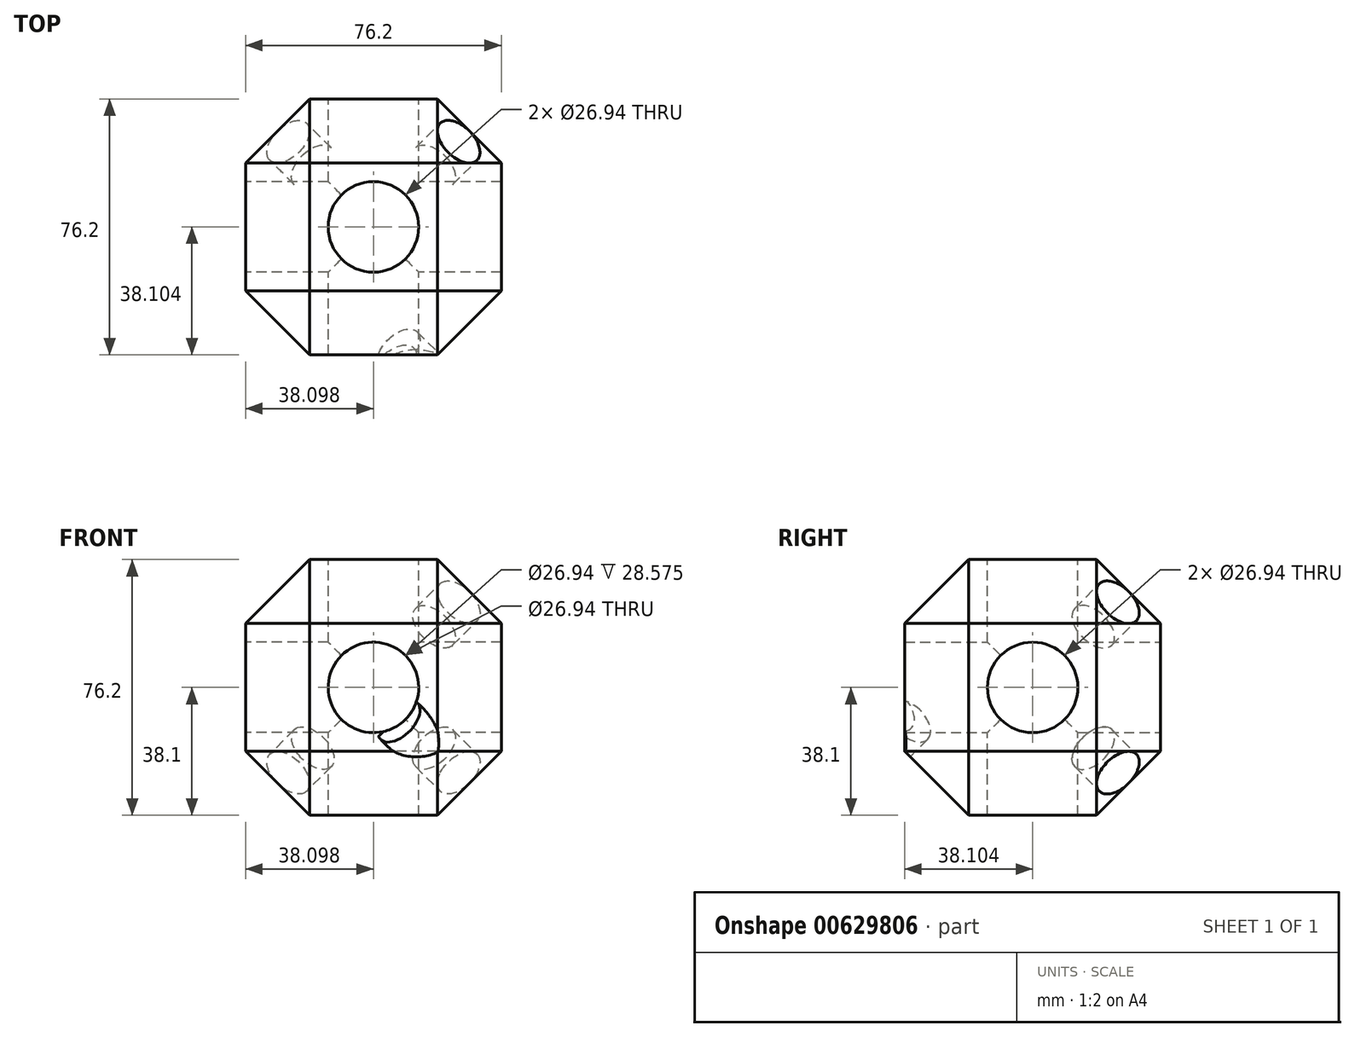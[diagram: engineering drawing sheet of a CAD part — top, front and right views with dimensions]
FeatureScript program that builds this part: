
annotation { "Feature Type Name" : "Feature", "Feature Type Description" : "" }
export const myFeature = defineFeature(function(context is Context, id is Id, definition is map)
    precondition{}
    {
        {
            var Q0;
            Q0=qCreatedBy(makeId("Top.planeOp"),FACE);
            var sketch = newSketch(context, id + "F0", { "sketchPlane" : qUnion([Q0])});
            skLineSegment(sketch, "E0.rect.bottom", {"start": v(29.23, 73.8) * mm, "end": v(-46.97, 73.8) * mm});
            skLineSegment(sketch, "E0.rect.top", {"start": v(29.23, -2.4) * mm, "end": v(-46.97, -2.4) * mm});
            skLineSegment(sketch, "E0.rect.left", {"start": v(29.23, 73.8) * mm, "end": v(29.23, -2.4) * mm});
            skLineSegment(sketch, "E0.rect.right", {"start": v(-46.97, 73.8) * mm, "end": v(-46.97, -2.4) * mm});
            skPoint(sketch, "E0.rect.middle", {"position": v(-8.87, 35.7) * mm});
            skSolve(sketch);
        }
        {
            var Q0;
            Q0=qSketchRegion(id+"F0",true);
            extrude(context, id + "F1", {"entities" : qUnion([Q0]), "depth" : 76.2 * mm});
        }
        {
            var Q0;
            Q0=makeQuery(id+"F1.opExtrude","SWEPT_FACE",FACE,{"disambiguationData":[OSD([sQuery(id+"F0.wireOp",EDGE,"E0.rect.right")])]});
            var Q1;
            Q1=makeQuery(id+"F1.opExtrude","SWEPT_FACE",FACE,{"disambiguationData":[OSD([sQuery(id+"F0.wireOp",EDGE,"E0.rect.bottom")])]});
            var Q2;
            Q2=makeQuery(id+"F1.opExtrude","SWEPT_FACE",FACE,{"disambiguationData":[OSD([sQuery(id+"F0.wireOp",EDGE,"E0.rect.top")])]});
            var Q3;
            Q3=makeQuery(id+"F1.opExtrude","CAP_FACE",FACE,{"disambiguationData":[OSD([sQuery(id+"F0.wireOp",EDGE,"E0.rect.bottom"),sQuery(id+"F0.wireOp",EDGE,"E0.rect.top"),sQuery(id+"F0.wireOp",EDGE,"E0.rect.left"),sQuery(id+"F0.wireOp",EDGE,"E0.rect.right")])],"isStart":true});
            var Q4;
            Q4=makeQuery(id+"F1.opExtrude","SWEPT_FACE",FACE,{"disambiguationData":[OSD([sQuery(id+"F0.wireOp",EDGE,"E0.rect.left")])]});
            chamfer(context, id + "F2", {"entities" : qUnion([Q0, Q1, Q2, Q3, Q4]), "width" : 19.05 * mm, "tangentPropagation" : true});
        }
        {
            var Q0;
            Q0=makeQuery(id+"F1.opExtrude","CAP_FACE",FACE,{"disambiguationData":[OSD([sQuery(id+"F0.wireOp",EDGE,"E0.rect.bottom"),sQuery(id+"F0.wireOp",EDGE,"E0.rect.top"),sQuery(id+"F0.wireOp",EDGE,"E0.rect.left"),sQuery(id+"F0.wireOp",EDGE,"E0.rect.right")])],"isStart":false});
            var sketch = newSketch(context, id + "F3", { "sketchPlane" : qUnion([Q0])});
            skCircle(sketch, "E1", {"center": v(-8.87, 35.7) * mm, "radius": 13.47 * mm});
            skPoint(sketch, "E1.first.point", {"position": v(-18.4, 45.22) * mm});
            skPoint(sketch, "E1.second.point", {"position": v(0.65, 45.22) * mm});
            skPoint(sketch, "E1.third.point", {"position": v(0.65, 26.17) * mm});
            skSolve(sketch);
        }
        {
            var Q0;
            Q0=qSketchRegion(id+"F3",true);
            extrude(context, id + "F4", {"entities" : qUnion([Q0]), "operationType" : NewBodyOperationType.REMOVE, "oppositeDirection" : true, "depth" : 127 * mm});
        }
        {
            var Q0;
            Q0=makeQuery(id+"F1.opExtrude","SWEPT_FACE",FACE,{"disambiguationData":[OSD([sQuery(id+"F0.wireOp",EDGE,"E0.rect.right")])]});
            var sketch = newSketch(context, id + "F5", { "sketchPlane" : qUnion([Q0])});
            skCircle(sketch, "E2", {"center": v(-35.7, 38.1) * mm, "radius": 13.47 * mm});
            skSolve(sketch);
        }
        {
            var Q0;
            Q0=qSketchRegion(id+"F5",true);
            var Q1;
            Q1=makeQuery(id+"F5.imprint","IMPRINT",FACE,{"disambiguationData":[TD([[makeQuery(id+"F5.imprint","IMPRINT",EDGE,{"derivedFrom":sQuery(id+"F5.wireOp",EDGE,"E2")}),1.0]])]});
            extrude(context, id + "F6", {"entities" : qUnion([Q0, Q1]), "operationType" : NewBodyOperationType.REMOVE, "oppositeDirection" : true, "depth" : 127 * mm});
        }
        {
            var Q0;
            Q0=makeQuery(id+"F1.opExtrude","SWEPT_FACE",FACE,{"disambiguationData":[OSD([sQuery(id+"F0.wireOp",EDGE,"E0.rect.bottom")])]});
            var sketch = newSketch(context, id + "F7", { "sketchPlane" : qUnion([Q0])});
            skCircle(sketch, "E3", {"center": v(8.87, 38.1) * mm, "radius": 13.47 * mm});
            skSolve(sketch);
        }
        {
            var Q0;
            Q0=qSketchRegion(id+"F7",true);
            extrude(context, id + "F8", {"entities" : qUnion([Q0]), "operationType" : NewBodyOperationType.REMOVE, "oppositeDirection" : true, "depth" : 127 * mm});
        }
        {
            var Q0;
            {var subQ0=sQuery(id+"F0.wireOp",EDGE,"E0.rect.bottom");var subQ1=sQuery(id+"F0.wireOp",EDGE,"E0.rect.left");Q0=makeQuery(id+"F2.opChamfer","BLEND_FACE",FACE,{"disambiguationData":[OSD([subQ0,subQ1]),TDD([makeQuery(id+"F1.opExtrude","CAP_VERTEX",VERTEX,{"disambiguationData":[OSD([subQ0,subQ1])],"isStart":true})])]});}
            var sketch = newSketch(context, id + "F9", { "sketchPlane" : qUnion([Q0])});
            skCircle(sketch, "E4", {"center": v(6.26, 52.18) * mm, "radius": 7.78 * mm});
            skPoint(sketch, "E4.first.point", {"position": v(2.37, 58.92) * mm});
            skPoint(sketch, "E4.second.point", {"position": v(14.04, 52.18) * mm});
            skPoint(sketch, "E4.third.point", {"position": v(2.37, 45.44) * mm});
            skSolve(sketch);
        }
        {
            var Q0;
            Q0=qSketchRegion(id+"F9",true);
            extrude(context, id + "F10", {"entities" : qUnion([Q0]), "operationType" : NewBodyOperationType.REMOVE, "oppositeDirection" : true, "depth" : 12.7 * mm});
        }
        {
            var Q0;
            {var subQ0=sQuery(id+"F0.wireOp",EDGE,"E0.rect.bottom");var subQ1=sQuery(id+"F0.wireOp",EDGE,"E0.rect.left");Q0=makeQuery(id+"F2.opChamfer","BLEND_FACE",FACE,{"disambiguationData":[OSD([subQ0,subQ1]),TDD([makeQuery(id+"F1.opExtrude","CAP_VERTEX",VERTEX,{"disambiguationData":[OSD([subQ0,subQ1])],"isStart":false})])]});}
            var sketch = newSketch(context, id + "F11", { "sketchPlane" : qUnion([Q0])});
            skCircle(sketch, "E5", {"center": v(37.37, 1.7) * mm, "radius": 7.78 * mm});
            skPoint(sketch, "E5.first.point", {"position": v(45.15, 1.7) * mm});
            skPoint(sketch, "E5.second.point", {"position": v(33.48, 8.44) * mm});
            skPoint(sketch, "E5.third.point", {"position": v(33.48, -5.03) * mm});
            skSolve(sketch);
        }
        {
            var Q0;
            {var subQ0=sQuery(id+"F11.wireOp",EDGE,"E5");var subQ1=sQuery(id+"F0.wireOp",EDGE,"E0.rect.bottom");var subQ2=sQuery(id+"F0.wireOp",EDGE,"E0.rect.left");var subQ3=makeQuery(id+"F1.opExtrude","CAP_VERTEX",VERTEX,{"disambiguationData":[OSD([subQ1,subQ2])],"isStart":false});var subQ6=makeQuery(id+"F11.imprint","INTERSECT",VERTEX,{"derivedFrom":[makeQuery(id+"F2.opChamfer","BLEND_EDGE",EDGE,{"blendedFrom":[subQ3,makeQuery(id+"F1.opExtrude","CAP_EDGE",EDGE,{"disambiguationData":[OSD([subQ2])],"isStart":false})],"blendedInto":[]}),subQ0]});Q0=makeQuery(id+"F11.imprint","IMPRINT",FACE,{"disambiguationData":[TD([[makeQuery(id+"F11.imprint","IMPRINT",EDGE,{"disambiguationData":[TD([[subQ6,1.0]])],"derivedFrom":subQ0}),1.0]])]});}
            extrude(context, id + "F12", {"entities" : qUnion([Q0]), "operationType" : NewBodyOperationType.REMOVE, "oppositeDirection" : true, "depth" : 12.7 * mm});
        }
        {
            var Q0;
            {var subQ0=sQuery(id+"F0.wireOp",EDGE,"E0.rect.bottom");var subQ1=sQuery(id+"F0.wireOp",EDGE,"E0.rect.right");Q0=makeQuery(id+"F2.opChamfer","BLEND_FACE",FACE,{"disambiguationData":[OSD([subQ0,subQ1]),TDD([makeQuery(id+"F1.opExtrude","CAP_VERTEX",VERTEX,{"disambiguationData":[OSD([subQ0,subQ1])],"isStart":false})])]});}
            var sketch = newSketch(context, id + "F13", { "sketchPlane" : qUnion([Q0])});
            skCircle(sketch, "E6", {"center": v(22.88, -1.7) * mm, "radius": 7.78 * mm});
            skPoint(sketch, "E6.first.point", {"position": v(19, -8.44) * mm});
            skPoint(sketch, "E6.second.point", {"position": v(19, 5.03) * mm});
            skPoint(sketch, "E6.third.point", {"position": v(30.66, -1.7) * mm});
            skSolve(sketch);
        }
        {
            var Q0;
            Q0=qSketchRegion(id+"F13",true);
            extrude(context, id + "F14", {"entities" : qUnion([Q0]), "operationType" : NewBodyOperationType.REMOVE, "oppositeDirection" : true, "depth" : 12.7 * mm});
        }
        {
            var Q0;
            {var subQ0=sQuery(id+"F0.wireOp",EDGE,"E0.rect.top");var subQ1=sQuery(id+"F0.wireOp",EDGE,"E0.rect.left");Q0=makeQuery(id+"F2.opChamfer","BLEND_FACE",FACE,{"disambiguationData":[OSD([subQ0,subQ1]),TDD([makeQuery(id+"F1.opExtrude","CAP_VERTEX",VERTEX,{"disambiguationData":[OSD([subQ0,subQ1])],"isStart":false})])]});}
            var sketch = newSketch(context, id + "F15", { "sketchPlane" : qUnion([Q0])});
            skCircle(sketch, "E7", {"center": v(41.08, 33.21) * mm, "radius": 7.78 * mm});
            skPoint(sketch, "E7.first.point", {"position": v(37.19, 39.95) * mm});
            skPoint(sketch, "E7.second.point", {"position": v(48.85, 33.21) * mm});
            skPoint(sketch, "E7.third.point", {"position": v(37.19, 26.48) * mm});
            skSolve(sketch);
        }
        {
            var Q0;
            {var subQ0=sQuery(id+"F15.wireOp",EDGE,"E7");var subQ1=sQuery(id+"F0.wireOp",EDGE,"E0.rect.top");var subQ2=sQuery(id+"F0.wireOp",EDGE,"E0.rect.left");var subQ3=makeQuery(id+"F1.opExtrude","CAP_VERTEX",VERTEX,{"disambiguationData":[OSD([subQ1,subQ2])],"isStart":false});var subQ6=makeQuery(id+"F15.imprint","INTERSECT",VERTEX,{"derivedFrom":[makeQuery(id+"F2.opChamfer","BLEND_EDGE",EDGE,{"blendedFrom":[subQ3,makeQuery(id+"F1.opExtrude","CAP_EDGE",EDGE,{"disambiguationData":[OSD([subQ1])],"isStart":false})],"blendedInto":[]}),subQ0]});Q0=makeQuery(id+"F15.imprint","IMPRINT",FACE,{"disambiguationData":[TD([[makeQuery(id+"F15.imprint","IMPRINT",EDGE,{"disambiguationData":[TD([[subQ6,1.0]])],"derivedFrom":subQ0}),1.0]])]});}
            extrude(context, id + "F16", {"entities" : qUnion([Q0]), "operationType" : NewBodyOperationType.REMOVE, "oppositeDirection" : true, "depth" : 12.7 * mm});
        }
        {
            var Q0;
            {var subQ0=sQuery(id+"F0.wireOp",EDGE,"E0.rect.top");var subQ1=sQuery(id+"F0.wireOp",EDGE,"E0.rect.left");Q0=makeQuery(id+"F2.opChamfer","BLEND_FACE",FACE,{"disambiguationData":[OSD([subQ0,subQ1]),TDD([makeQuery(id+"F1.opExtrude","CAP_VERTEX",VERTEX,{"disambiguationData":[OSD([subQ0,subQ1])],"isStart":true})])]});}
            var sketch = newSketch(context, id + "F17", { "sketchPlane" : qUnion([Q0])});
            skCircle(sketch, "E8", {"center": v(9.97, 20.67) * mm, "radius": 7.78 * mm});
            skPoint(sketch, "E8.first.point", {"position": v(17.74, 20.67) * mm});
            skPoint(sketch, "E8.second.point", {"position": v(6.08, 13.93) * mm});
            skPoint(sketch, "E8.third.point", {"position": v(6.08, 27.4) * mm});
            skSolve(sketch);
        }
        {
            var Q0;
            {var subQ0=sQuery(id+"F17.wireOp",EDGE,"E8");var subQ1=sQuery(id+"F0.wireOp",EDGE,"E0.rect.top");var subQ2=sQuery(id+"F0.wireOp",EDGE,"E0.rect.left");var subQ3=makeQuery(id+"F1.opExtrude","CAP_VERTEX",VERTEX,{"disambiguationData":[OSD([subQ1,subQ2])],"isStart":true});var subQ5=makeQuery(id+"F17.imprint","INTERSECT",VERTEX,{"derivedFrom":[makeQuery(id+"F2.opChamfer","BLEND_EDGE",EDGE,{"blendedFrom":[subQ3,makeQuery(id+"F1.opExtrude","CAP_EDGE",EDGE,{"disambiguationData":[OSD([subQ2])],"isStart":true})],"blendedInto":[]}),subQ0]});Q0=makeQuery(id+"F17.imprint","IMPRINT",FACE,{"disambiguationData":[TD([[makeQuery(id+"F17.imprint","IMPRINT",EDGE,{"disambiguationData":[TD([[subQ5,1.0]])],"derivedFrom":subQ0}),1.0]])]});}
            extrude(context, id + "F18", {"entities" : qUnion([Q0]), "operationType" : NewBodyOperationType.REMOVE, "oppositeDirection" : true, "depth" : 12.7 * mm});
        }
        {
            var Q0;
            {var subQ0=sQuery(id+"F0.wireOp",EDGE,"E0.rect.top");var subQ1=sQuery(id+"F0.wireOp",EDGE,"E0.rect.right");Q0=makeQuery(id+"F2.opChamfer","BLEND_FACE",FACE,{"disambiguationData":[OSD([subQ0,subQ1]),TDD([makeQuery(id+"F1.opExtrude","CAP_VERTEX",VERTEX,{"disambiguationData":[OSD([subQ0,subQ1])],"isStart":true})])]});}
            var sketch = newSketch(context, id + "F19", { "sketchPlane" : qUnion([Q0])});
            skCircle(sketch, "E9", {"center": v(-17.21, 33.21) * mm, "radius": 7.78 * mm});
            skPoint(sketch, "E9.first.point", {"position": v(-13.32, 26.48) * mm});
            skPoint(sketch, "E9.second.point", {"position": v(-24.99, 33.21) * mm});
            skPoint(sketch, "E9.third.point", {"position": v(-13.32, 39.95) * mm});
            skSolve(sketch);
        }
        {
            var Q0;
            {var subQ0=sQuery(id+"F19.wireOp",EDGE,"E9");var subQ1=sQuery(id+"F0.wireOp",EDGE,"E0.rect.top");var subQ2=sQuery(id+"F0.wireOp",EDGE,"E0.rect.right");var subQ3=makeQuery(id+"F1.opExtrude","CAP_VERTEX",VERTEX,{"disambiguationData":[OSD([subQ1,subQ2])],"isStart":true});var subQ6=makeQuery(id+"F19.imprint","INTERSECT",VERTEX,{"derivedFrom":[makeQuery(id+"F2.opChamfer","BLEND_EDGE",EDGE,{"blendedFrom":[subQ3,makeQuery(id+"F1.opExtrude","CAP_EDGE",EDGE,{"disambiguationData":[OSD([subQ2])],"isStart":true})],"blendedInto":[]}),subQ0]});Q0=makeQuery(id+"F19.imprint","IMPRINT",FACE,{"disambiguationData":[TD([[makeQuery(id+"F19.imprint","IMPRINT",EDGE,{"disambiguationData":[TD([[subQ6,-1.0]])],"derivedFrom":subQ0}),1.0]])]});}
            extrude(context, id + "F20", {"entities" : qUnion([Q0]), "operationType" : NewBodyOperationType.REMOVE, "oppositeDirection" : true, "depth" : 12.7 * mm});
        }
        {
            var Q0;
            {var subQ0=sQuery(id+"F0.wireOp",EDGE,"E0.rect.top");var subQ1=sQuery(id+"F0.wireOp",EDGE,"E0.rect.right");Q0=makeQuery(id+"F2.opChamfer","BLEND_FACE",FACE,{"disambiguationData":[OSD([subQ0,subQ1]),TDD([makeQuery(id+"F1.opExtrude","CAP_VERTEX",VERTEX,{"disambiguationData":[OSD([subQ0,subQ1])],"isStart":false})])]});}
            var sketch = newSketch(context, id + "F21", { "sketchPlane" : qUnion([Q0])});
            skCircle(sketch, "E10", {"center": v(-48.32, 20.67) * mm, "radius": 7.78 * mm});
            skPoint(sketch, "E10.first.point", {"position": v(-44.43, 13.93) * mm});
            skPoint(sketch, "E10.second.point", {"position": v(-44.43, 27.4) * mm});
            skPoint(sketch, "E10.third.point", {"position": v(-56.1, 20.67) * mm});
            skSolve(sketch);
        }
        {
            var Q0;
            {var subQ0=sQuery(id+"F21.wireOp",EDGE,"E10");var subQ1=sQuery(id+"F0.wireOp",EDGE,"E0.rect.top");var subQ2=sQuery(id+"F0.wireOp",EDGE,"E0.rect.right");var subQ3=makeQuery(id+"F1.opExtrude","CAP_VERTEX",VERTEX,{"disambiguationData":[OSD([subQ1,subQ2])],"isStart":false});var subQ6=makeQuery(id+"F21.imprint","INTERSECT",VERTEX,{"derivedFrom":[makeQuery(id+"F2.opChamfer","BLEND_EDGE",EDGE,{"blendedFrom":[subQ3,makeQuery(id+"F1.opExtrude","CAP_EDGE",EDGE,{"disambiguationData":[OSD([subQ2])],"isStart":false})],"blendedInto":[]}),subQ0]});Q0=makeQuery(id+"F21.imprint","IMPRINT",FACE,{"disambiguationData":[TD([[makeQuery(id+"F21.imprint","IMPRINT",EDGE,{"disambiguationData":[TD([[subQ6,1.0]])],"derivedFrom":subQ0}),1.0]])]});}
            extrude(context, id + "F22", {"entities" : qUnion([Q0]), "operationType" : NewBodyOperationType.REMOVE, "oppositeDirection" : true, "depth" : 12.7 * mm});
        }
        {
            var Q0;
            {var subQ0=sQuery(id+"F0.wireOp",EDGE,"E0.rect.bottom");var subQ1=sQuery(id+"F0.wireOp",EDGE,"E0.rect.right");Q0=makeQuery(id+"F2.opChamfer","BLEND_FACE",FACE,{"disambiguationData":[OSD([subQ0,subQ1]),TDD([makeQuery(id+"F1.opExtrude","CAP_VERTEX",VERTEX,{"disambiguationData":[OSD([subQ0,subQ1])],"isStart":true})])]});}
            var sketch = newSketch(context, id + "F23", { "sketchPlane" : qUnion([Q0])});
            skCircle(sketch, "E11", {"center": v(8.23, 52.18) * mm, "radius": 7.78 * mm});
            skPoint(sketch, "E11.first.point", {"position": v(12.11, 45.44) * mm});
            skPoint(sketch, "E11.second.point", {"position": v(0.45, 52.18) * mm});
            skPoint(sketch, "E11.third.point", {"position": v(12.11, 58.92) * mm});
            skSolve(sketch);
        }
        {
            var Q0;
            {var subQ0=sQuery(id+"F23.wireOp",EDGE,"E11");var subQ1=sQuery(id+"F0.wireOp",EDGE,"E0.rect.bottom");var subQ2=sQuery(id+"F0.wireOp",EDGE,"E0.rect.right");var subQ3=makeQuery(id+"F1.opExtrude","CAP_VERTEX",VERTEX,{"disambiguationData":[OSD([subQ1,subQ2])],"isStart":true});var subQ6=makeQuery(id+"F23.imprint","INTERSECT",VERTEX,{"derivedFrom":[makeQuery(id+"F2.opChamfer","BLEND_EDGE",EDGE,{"blendedFrom":[subQ3,makeQuery(id+"F1.opExtrude","CAP_EDGE",EDGE,{"disambiguationData":[OSD([subQ1])],"isStart":true})],"blendedInto":[]}),subQ0]});Q0=makeQuery(id+"F23.imprint","IMPRINT",FACE,{"disambiguationData":[TD([[makeQuery(id+"F23.imprint","IMPRINT",EDGE,{"disambiguationData":[TD([[subQ6,-1.0]])],"derivedFrom":subQ0}),1.0]])]});}
            extrude(context, id + "F24", {"entities" : qUnion([Q0]), "operationType" : NewBodyOperationType.REMOVE, "oppositeDirection" : true, "depth" : 12.7 * mm});
        }
    });
